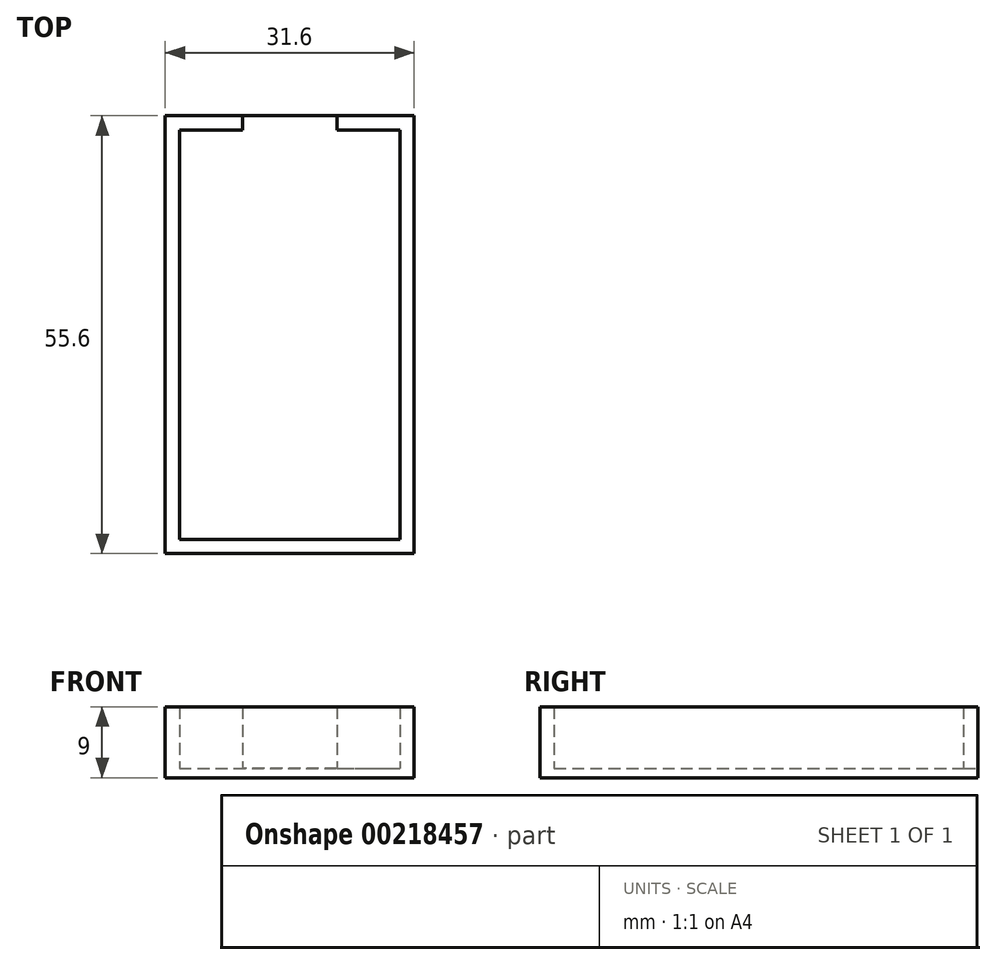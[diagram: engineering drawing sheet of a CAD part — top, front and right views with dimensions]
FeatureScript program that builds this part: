
annotation { "Feature Type Name" : "Feature", "Feature Type Description" : "" }
export const myFeature = defineFeature(function(context is Context, id is Id, definition is map)
    precondition{}
    {
        {
            var Q0;
            Q0=qCreatedBy(makeId("Top.planeOp"),FACE);
            var sketch = newSketch(context, id + "F0", { "sketchPlane" : qUnion([Q0])});
            skLineSegment(sketch, "E0.bottom", {"start": v(14, 26) * mm, "end": v(-14, 26) * mm});
            skLineSegment(sketch, "E0.top", {"start": v(14, -26) * mm, "end": v(-14, -26) * mm});
            skLineSegment(sketch, "E0.left", {"start": v(14, 26) * mm, "end": v(14, -26) * mm});
            skLineSegment(sketch, "E0.right", {"start": v(-14, 26) * mm, "end": v(-14, -26) * mm});
            skPoint(sketch, "E0.middle", {"position": v(0, 0) * mm});
            skLineSegment(sketch, "E1.0", {"start": v(-15.8, 27.8) * mm, "end": v(-15.8, -27.8) * mm});
            skLineSegment(sketch, "E1.1", {"start": v(15.8, 27.8) * mm, "end": v(-15.8, 27.8) * mm});
            skLineSegment(sketch, "E1.2", {"start": v(15.8, 27.8) * mm, "end": v(15.8, -27.8) * mm});
            skLineSegment(sketch, "E1.3", {"start": v(15.8, -27.8) * mm, "end": v(-15.8, -27.8) * mm});
            skLineSegment(sketch, "E2.bottom", {"start": v(6, 27.8) * mm, "end": v(-6, 27.8) * mm});
            skLineSegment(sketch, "E2.left", {"start": v(6, 27.8) * mm, "end": v(6, 26) * mm});
            skLineSegment(sketch, "E2.right", {"start": v(-6, 27.8) * mm, "end": v(-6, 26) * mm});
            skPoint(sketch, "E2.middle", {"position": v(0, 26) * mm});
            skPoint(sketch, "E3.orphan", {"position": v(6, 24.2) * mm});
            skPoint(sketch, "E4.orphan", {"position": v(-6, 24.2) * mm});
            skSolve(sketch);
        }
        {
            var Q0;
            Q0 = qSketchRegion(id + "F0", true);
            var Q1;
            Q1=makeQuery(id+"F0.imprint","IMPRINT",FACE,{"disambiguationData":[TD([[makeQuery(id+"F0.imprint","IMPRINT",EDGE,{"derivedFrom":sQuery(id+"F0.wireOp",EDGE,"E0.top")}),-1.0]])]});
            extrude(context, id + "F1", {"entities" : qUnion([Q0, Q1]), "depth" : 1.2 * mm});
        }
        {
            var Q0;
            Q0=makeQuery(id+"F0.imprint","IMPRINT",FACE,{"disambiguationData":[TD([[makeQuery(id+"F0.imprint","IMPRINT",EDGE,{"derivedFrom":sQuery(id+"F0.wireOp",EDGE,"E0.top")}),1.0]])]});
            extrude(context, id + "F2", {"entities" : qUnion([Q0]), "operationType" : NewBodyOperationType.ADD, "depth" : 9 * mm});
        }
    });
